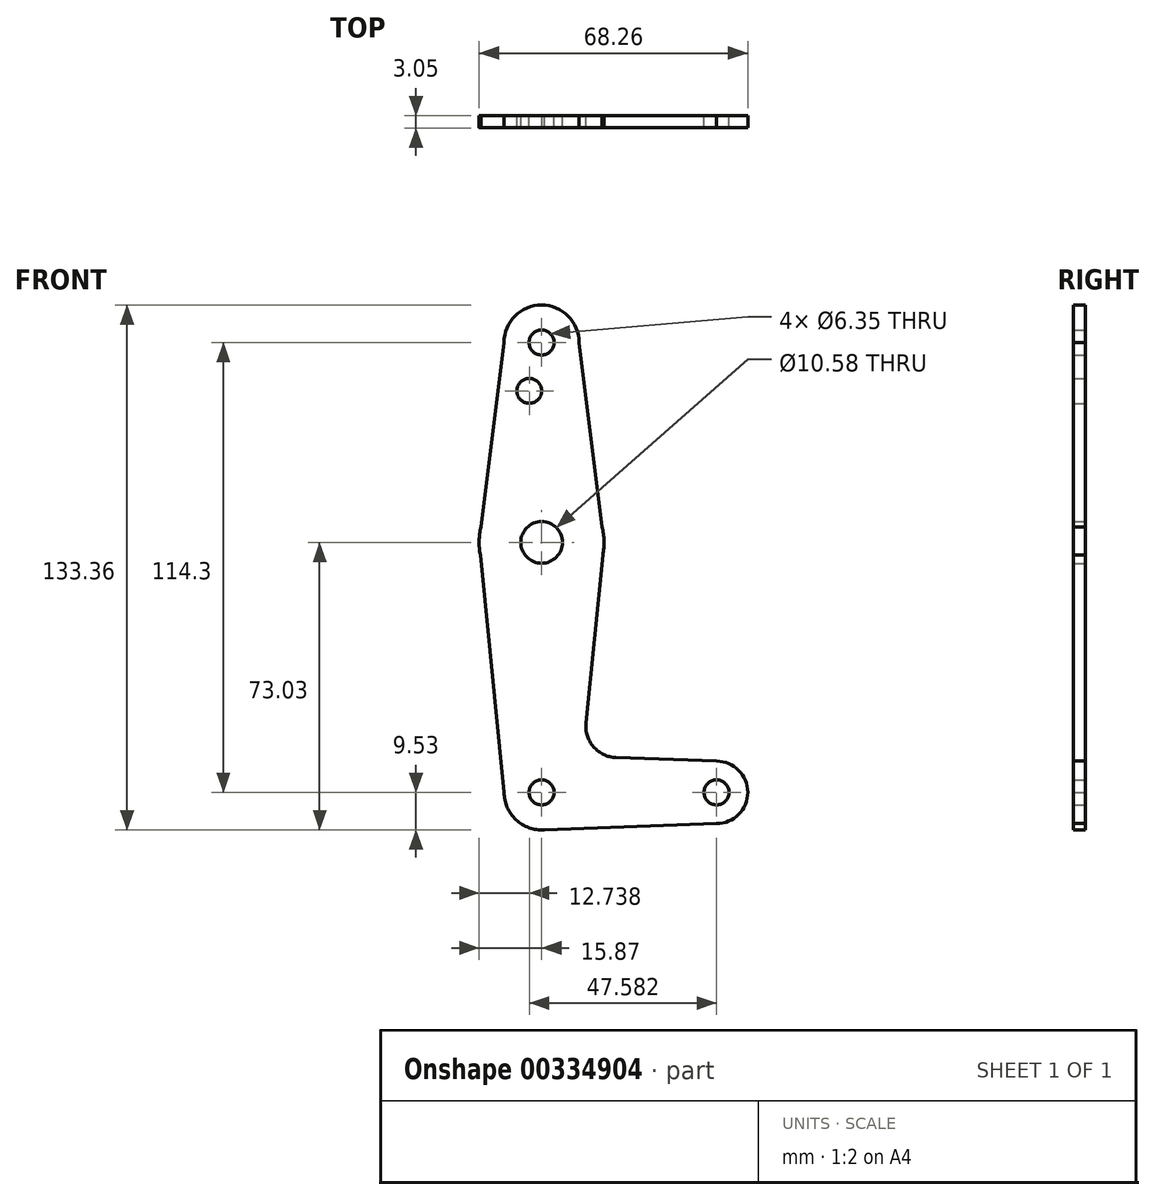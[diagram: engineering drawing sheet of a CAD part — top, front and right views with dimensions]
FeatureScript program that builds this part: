
annotation { "Feature Type Name" : "Feature", "Feature Type Description" : "" }
export const myFeature = defineFeature(function(context is Context, id is Id, definition is map)
    precondition{}
    {
        {
            var Q0;
            Q0=qCreatedBy(makeId("Front.planeOp"),FACE);
            var sketch = newSketch(context, id + "F0", { "sketchPlane" : qUnion([Q0])});
            skLineSegment(sketch, "E0", {"start": v(0, 0) * mm, "end": v(0, 114.3) * mm, "construction": true});
            skLineSegment(sketch, "E1", {"start": v(0, 0) * mm, "end": v(44.45, 0) * mm, "construction": true});
            skCircle(sketch, "E2", {"center": v(0, 114.3) * mm, "radius": 9.53 * mm});
            skCircle(sketch, "E3", {"center": v(0, 63.5) * mm, "radius": 15.88 * mm});
            skCircle(sketch, "E4", {"center": v(0, 0) * mm, "radius": 9.53 * mm});
            skCircle(sketch, "E5", {"center": v(44.45, 0) * mm, "radius": 7.94 * mm});
            skLineSegment(sketch, "E6", {"start": v(-15.88, 63.5) * mm, "end": v(-9.52, 114.3) * mm});
            skPoint(sketch, "E7.orphan", {"position": v(9.52, 114.3) * mm});
            skLineSegment(sketch, "E8", {"start": v(15.88, 63.5) * mm, "end": v(9.52, 114.3) * mm});
            skLineSegment(sketch, "E9", {"start": v(-15.88, 63.5) * mm, "end": v(-9.52, 0) * mm});
            skLineSegment(sketch, "E10", {"start": v(11.28, 17.59) * mm, "end": v(15.88, 63.5) * mm});
            skLineSegment(sketch, "E11", {"start": v(0, -9.53) * mm, "end": v(44.45, -7.94) * mm});
            skPoint(sketch, "E12.orphan", {"position": v(44.45, 7.94) * mm});
            skLineSegment(sketch, "E13", {"start": v(44.45, 7.94) * mm, "end": v(18.91, 8.85) * mm});
            skCircle(sketch, "E14", {"center": v(-3.13, 102.01) * mm, "radius": 3.18 * mm});
            skCircle(sketch, "E15", {"center": v(0, 63.5) * mm, "radius": 5.29 * mm});
            skArc(sketch, "E16.filletArc", {"start": v(11.28, 17.59) * mm, "mid": v(13.2, 11.57) * mm, "end": v(18.91, 8.85) * mm});
            skCircle(sketch, "E17", {"center": v(0, 114.3) * mm, "radius": 3.18 * mm});
            skCircle(sketch, "E18", {"center": v(44.45, 0) * mm, "radius": 3.18 * mm});
            skCircle(sketch, "E19", {"center": v(0, 0) * mm, "radius": 3.18 * mm});
            skSolve(sketch);
        }
        {
            var Q0;
            Q0 = qSketchRegion(id + "F0", true);
            extrude(context, id + "F1", {"entities" : qUnion([Q0]), "depth" : 3.05 * mm});
        }
    });
